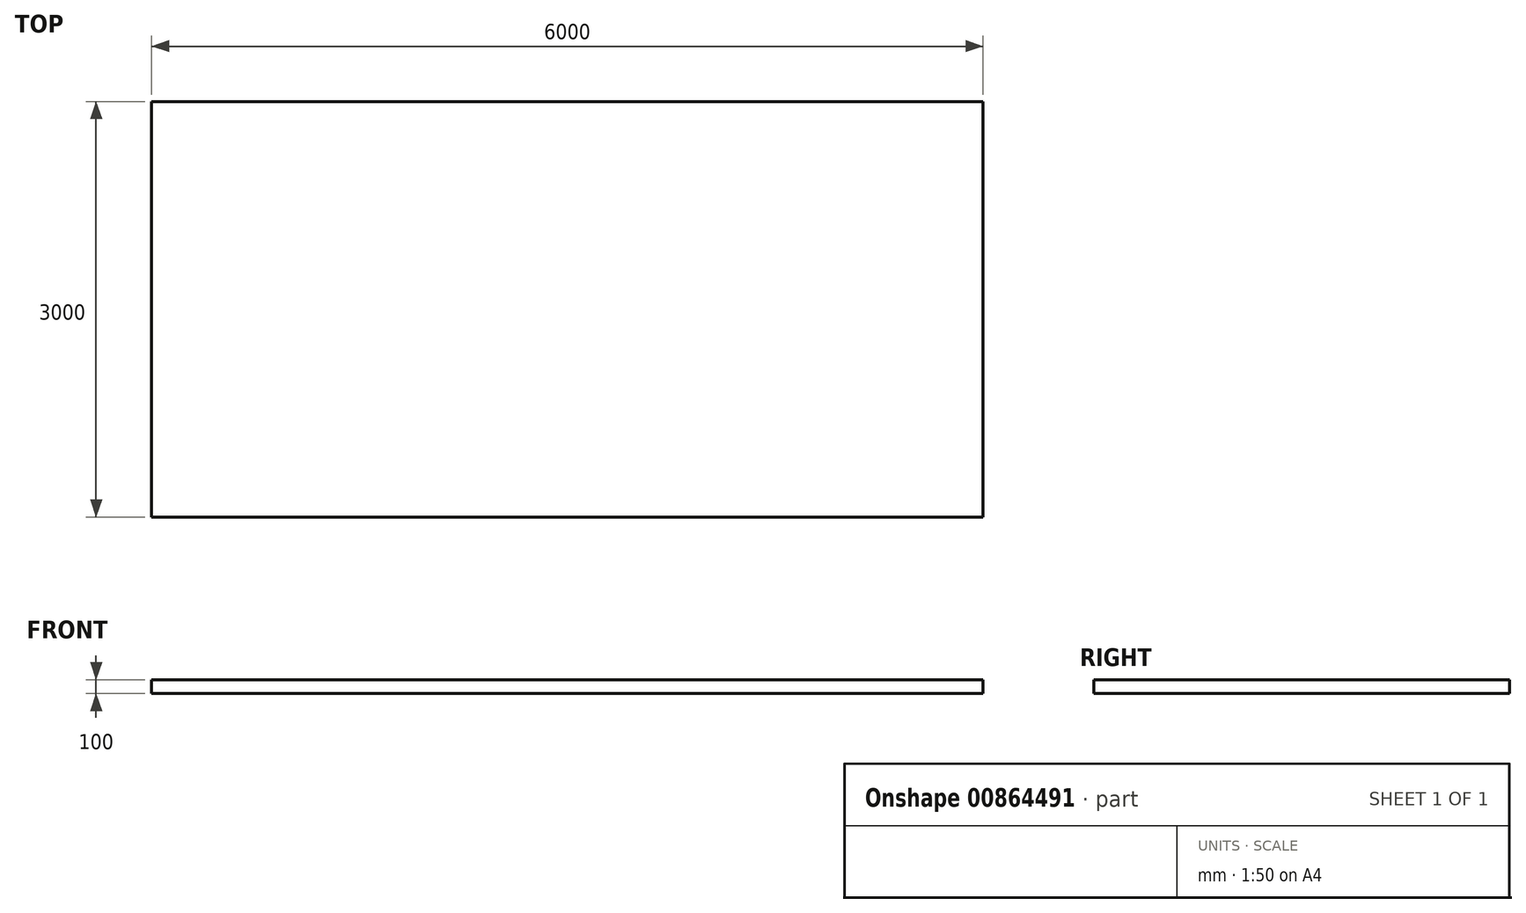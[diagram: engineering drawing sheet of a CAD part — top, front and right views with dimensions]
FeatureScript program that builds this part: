
annotation { "Feature Type Name" : "Feature", "Feature Type Description" : "" }
export const myFeature = defineFeature(function(context is Context, id is Id, definition is map)
    precondition{}
    {
        {
            var Q0;
            Q0=qCreatedBy(makeId("Top.planeOp"),FACE);
            var sketch = newSketch(context, id + "F0", { "sketchPlane" : qUnion([Q0])});
            skLineSegment(sketch, "E0.bottom", {"start": v(0, 0) * mm, "end": v(6000, 0) * mm});
            skLineSegment(sketch, "E0.top", {"start": v(0, 3000) * mm, "end": v(6000, 3000) * mm});
            skLineSegment(sketch, "E0.left", {"start": v(0, 0) * mm, "end": v(0, 3000) * mm});
            skLineSegment(sketch, "E0.right", {"start": v(6000, 0) * mm, "end": v(6000, 3000) * mm});
            skSolve(sketch);
        }
        {
            var Q0;
            Q0=makeQuery(id+"F0.imprint","IMPRINT",FACE,{"disambiguationData":[TD([[makeQuery(id+"F0.imprint","IMPRINT",EDGE,{"derivedFrom":sQuery(id+"F0.wireOp",EDGE,"E0.bottom")}),1.0]])]});
            extrude(context, id + "F1", {"entities" : qUnion([Q0]), "depth" : 100 * mm, "offsetDistance" : 25 * mm});
        }
    });
